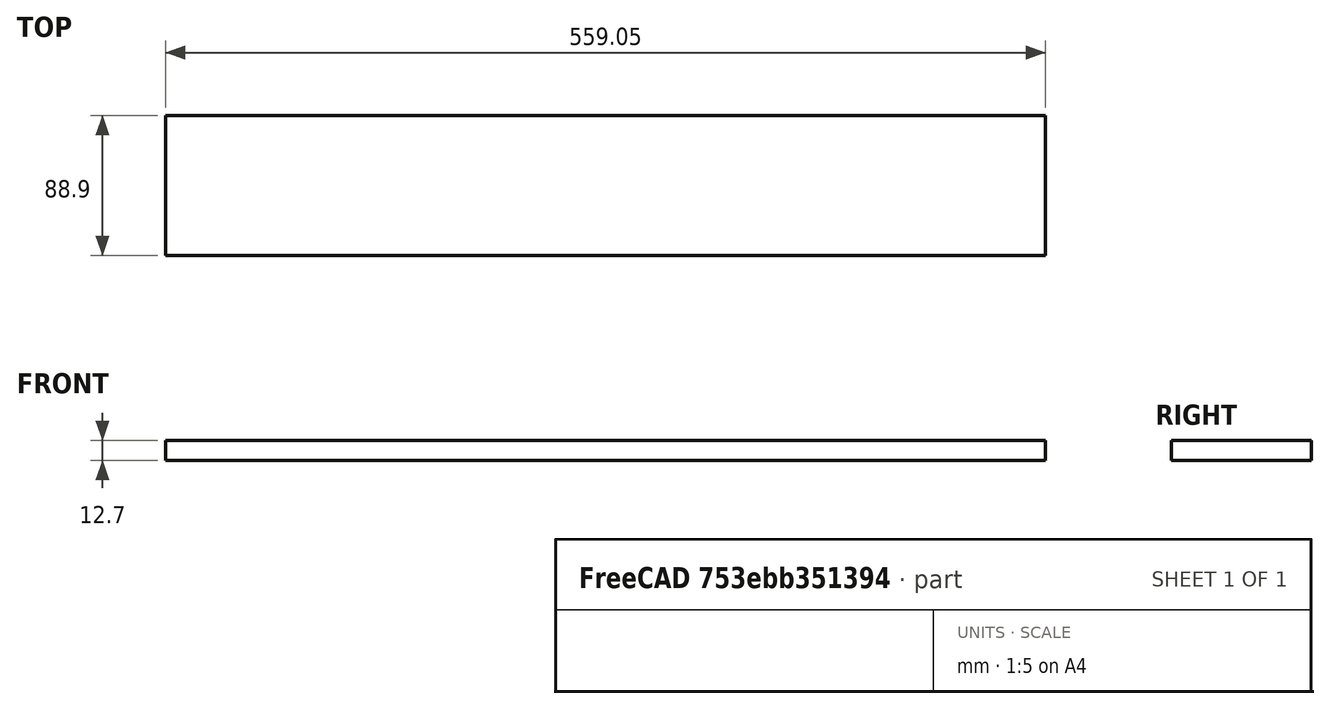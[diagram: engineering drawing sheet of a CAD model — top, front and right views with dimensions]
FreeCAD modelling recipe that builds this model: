
FCSTD DOCUMENT  (FreeCAD 0.19R24291 (Git))
Label: bottom3
License: All rights reserved
LicenseURL: http://en.wikipedia.org/wiki/All_rights_reserved
objects: Sketcher::SketchObject×1, PartDesign::Pad×1, PartDesign::Body×1
note: 4 computed .brp shape members not serialized (recipe doc carries the construction recipe); baked Part::Feature solids carry a one-line shape summary decoded from their .brp

FEATURE [Sketcher::SketchObject] Sketch
  FullyConstrained = true
  MapMode = 5
  Support = -> [XY_Plane]
  expr: Constraints[10] = 540 + 3 / 4 * 25.4
  expr: Constraints[8] = 3.5 * 25.4
  sketch-geometry (4):
    g0: LineSegment StartX=0 StartY=88.9 StartZ=0 EndX=559.05 EndY=88.9 EndZ=0
    g1: LineSegment StartX=559.05 StartY=88.9 StartZ=0 EndX=559.05 EndY=0 EndZ=0
    g2: LineSegment StartX=559.05 StartY=0 StartZ=0 EndX=0 EndY=0 EndZ=0
    g3: LineSegment StartX=0 StartY=0 StartZ=0 EndX=0 EndY=88.9 EndZ=0
  constraints (11):
    c: Coincident(g0,g1)
    c: Coincident(g1,g2)
    c: Coincident(g2,g3)
    c: Coincident(g3,g0)
    c: Horizontal(g0)
    c: Horizontal(g2)
    c: Vertical(g1)
    c: Vertical(g3)
    c: DistanceY(g3,g3) = 88.9
    c: Coincident(g2,g-1)
    c: DistanceX(g2,g1) = 559.05
FEATURE [PartDesign::Pad] Pad
  Direction = (1,1,1)
  Length = 12.7
  Length2 = 100
  Profile = -> Sketch
  Type = 0
  expr: Length = 1 / 2 * 25.4
FEATURE [PartDesign::Body] Body
  Group = -> [Sketch,Pad]
  Origin = -> Origin
  Tip = -> Pad
